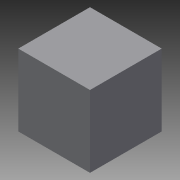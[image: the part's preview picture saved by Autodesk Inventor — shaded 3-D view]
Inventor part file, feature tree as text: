
AUTODESK INVENTOR PART (.ipt)
format: ipt  version: 2014 (Build 180170000, 170)  size: 88,576 bytes
history: native  units: mm
features: other x48, extrude x1, sketch x1
ambient origin geometry x8: Origin, YZ Plane, XZ Plane, XY Plane, X Axis, Y Axis, Z Axis, Center Point
bodies: 实体1 (feature_tree)
feature tree (50):
  extrude  "拉伸1"  [1 undecoded]
  other  "UCS1"
  other  "UCS2"
  other  "UCS3"
  other  "UCS4"
  other  "UCS5"
  other  "UCS6"
  sketch  "草图1"  dims[d0=200.0mm d1=0.0mm d2=0.0mm d3=0.0mm d4=0.0mm d5=0.0mm d6=0.0mm d7=0.0mm d8=0.0mm d9=0.0mm d10=0.0mm d11=0.0mm d12=0.0mm d13=0.0mm d14=0.0mm d15=0.0mm d16=0.0mm d17=0.0mm d18=0.0mm d19=0.0mm d20=0.0mm d21=0.0mm d22=0.0mm d23=0.0mm d24=0.0mm d25=0.0mm d26=0.0mm d27=0.0mm d28=0.0mm d29=0.0mm d30=0.0mm d31=0.0mm d32=0.0mm d33=0.0mm d34=0.0mm d35=0.0mm d36=0.0mm d37=0.0mm]
  other  "UCS1: YZ 平面"
  other  "UCS1: XZ 平面"
  other  "UCS1: XY 平面"
  other  "UCS1: X 轴"
  other  "UCS1: Y 轴"
  other  "UCS1: Z 轴"
  other  "UCS1: 原点"
  other  "UCS2: YZ 平面"
  other  "UCS2: XZ 平面"
  other  "UCS2: XY 平面"
  other  "UCS2: X 轴"
  other  "UCS2: Y 轴"
  other  "UCS2: Z 轴"
  other  "UCS2: 原点"
  other  "UCS3: YZ 平面"
  other  "UCS3: XZ 平面"
  other  "UCS3: XY 平面"
  other  "UCS3: X 轴"
  other  "UCS3: Y 轴"
  other  "UCS3: Z 轴"
  other  "UCS3: 原点"
  other  "UCS4: YZ 平面"
  other  "UCS4: XZ 平面"
  other  "UCS4: XY 平面"
  other  "UCS4: X 轴"
  other  "UCS4: Y 轴"
  other  "UCS4: Z 轴"
  other  "UCS4: 原点"
  other  "UCS5: YZ 平面"
  other  "UCS5: XZ 平面"
  other  "UCS5: XY 平面"
  other  "UCS5: X 轴"
  other  "UCS5: Y 轴"
  other  "UCS5: Z 轴"
  other  "UCS5: 原点"
  other  "UCS6: YZ 平面"
  other  "UCS6: XZ 平面"
  other  "UCS6: XY 平面"
  other  "UCS6: X 轴"
  other  "UCS6: Y 轴"
  other  "UCS6: Z 轴"
  other  "UCS6: 原点"
note: 1 required parameter value undecoded (feature->parameter linkage not recoverable at this tier; creation-order binding heuristic only, values carry confidence <= 0.55)
